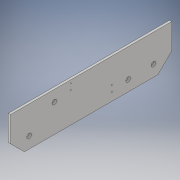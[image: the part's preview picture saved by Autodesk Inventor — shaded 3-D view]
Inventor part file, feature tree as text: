
AUTODESK INVENTOR PART (.ipt)
format: ipt  version: 2017 (Build 210142000, 142)  size: 151,040 bytes
history: native  units: in
note: dims shown in document units (in); Inventor stores cm internally (conversion verified against a paired STEP export)
features: extrude x3, sketch x3, chamfer x2, projected_geometry x2
ambient origin geometry x8: Origin, YZ Plane, XZ Plane, XY Plane, X Axis, Y Axis, Z Axis, Center Point
bodies: Solid1 (feature_tree)
feature tree (10):
  extrude  "Extrusion1"  Depth=17.5in
  chamfer  "Chamfer1"  Distance=2.0in
  chamfer  "Chamfer2"  Distance=2.0in
  extrude  "Extrusion2"  Depth=0.25in TaperAngle=0.0deg
  extrude  "Extrusion3"  Depth=0.25in TaperAngle=45.0deg
  sketch  "Sketch1"  dims[d0=4.25in d1=17.5in]
  sketch  "Sketch2"  dims[d2=0.501in]
  projected_geometry  "Projected Loop1"
  sketch  "Sketch3"  dims[d3=1.25in d4=2.0in d5=2.0in d6=0.25in d7=0.0in d8=1.5in d9=0.125in d10=45.0deg d11=1.5in d12=0.125in d13=45.0deg d14=0.501in d15=4.741in d16=1.181in d17=0.501in d18=1.181in d19=4.741in d20=1.0in d21=0.0in d22=6.517in d23=0.125in d24=0.603in d25=0.125in d26=0.63in d27=6.517in d28=0.125in d29=0.603in d30=6.517in d31=0.125in d32=0.63in d33=6.517in d34=0.125in d35=6.517in d36=0.315in d37=0.125in d38=0.63in d39=0.125in d40=0.125in d41=0.9in d42=0.63in d43=6.517in d44=1.0in d45=0.0in]
  projected_geometry  "Projected Loop2"
